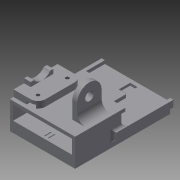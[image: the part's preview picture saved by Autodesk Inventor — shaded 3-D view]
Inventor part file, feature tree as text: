
AUTODESK INVENTOR PART (.ipt)
format: ipt  version: 2014 SP1 (Build 180222100, 222)  size: 471,040 bytes
history: native  units: mm
features: extrude x23, sketch x22, mirror x6, fillet x6, plane x2, hole x1, chamfer x1
ambient origin geometry x8: Origin, YZ Plane, XZ Plane, XY Plane, X Axis, Y Axis, Z Axis, Center Point
bodies: Solid1 (feature_tree)
feature tree (61):
  extrude  "Extrusion1"  Depth=40.0mm
  extrude  "Extrusion2"  Depth=10.0mm
  extrude  "Extrusion3"  Depth=8.5mm TaperAngle=0.0deg
  mirror  "Mirror1"
  extrude  "Extrusion4"  Depth=2.0mm TaperAngle=0.0deg
  mirror  "Mirror2"
  extrude  "Extrusion5"  Depth=2.0mm TaperAngle=0.0deg
  extrude  "Extrusion6"  Depth=12.5mm
  extrude  "Extrusion7"  Depth=12.5mm
  fillet  "Fillet1"  Radius=18.25mm
  extrude  "Extrusion8"  Depth=15.0mm
  plane  "Work Plane1"
  extrude  "Extrusion9"  Depth=5.0mm
  plane  "Work Plane2"
  mirror  "Mirror3"
  hole  "Hole1"  [1 undecoded]
  extrude  "Extrusion10"  Depth=7.5mm
  extrude  "Extrusion11"  Depth=7.5mm
  extrude  "Extrusion12"  Depth=5.0mm
  mirror  "Mirror4"
  fillet  "Fillet2"  Radius=4.0mm
  fillet  "Fillet3"  [1 undecoded]
  fillet  "Fillet4"  Radius=5.0mm
  extrude  "Extrusion13"  Depth=4.5mm
  sketch  "Sketch16"  dims[d45=4.5mm d46=9.0mm]
  extrude  "Extrusion14"  Depth=4.5mm
  extrude  "Extrusion15"  Depth=2.0mm
  extrude  "Extrusion17"  Depth=10.0mm TaperAngle=0.0deg
  extrude  "Extrusion16"  Depth=5.0mm TaperAngle=0.0deg
  chamfer  "Chamfer1"  Distance=2.0mm
  mirror  "Mirror5"
  extrude  "Extrusion18"  Depth=5.0mm
  extrude  "Extrusion19"  Depth=20.0mm TaperAngle=0.0deg
  fillet  "Fillet5"  Radius=37.0mm
  extrude  "Extrusion20"  Depth=40.0mm
  extrude  "Extrusion21"  Depth=1.5mm
  extrude  "Extrusion22"  Depth=4.5mm TaperAngle=0.0deg
  mirror  "Mirror6"
  fillet  "Fillet6"  Radius=4.5mm
  extrude  "Extrusion23"  Depth=15.0mm
  sketch  "Sketch1"  dims[d0=40.0mm d2=6.35mm]
  sketch  "Sketch2"  dims[d4=9.5mm d5=10.0mm]
  sketch  "Sketch4"  dims[d6=20.0mm d7=8.5mm d8=0.0mm]
  sketch  "Sketch5"  dims[d9=20.0mm d10=2.0mm d11=0.0mm]
  sketch  "Sketch6"  dims[d12=6.35mm d13=2.0mm d14=0.0mm]
  sketch  "Sketch7"  dims[d15=7.0mm d17=12.5mm]
  sketch  "Sketch9"  dims[d18=2.0mm d19=0.0mm d20=12.5mm d21=18.25mm d22=0.0mm]
  sketch  "Sketch10"  dims[d23=15.0mm d25=3.0mm]
  sketch  "Sketch11"  dims[d26=4.5mm d27=5.0mm]
  sketch  "Sketch12"  dims[d28=14.5mm d29=17.5mm d30=0.0mm]
  sketch  "Sketch13"  dims[d31=5.1mm d34=7.5mm]
  sketch  "Sketch14"  dims[d35=10.0mm d36=0.0mm d37=7.5mm]
  sketch  "Sketch15"  dims[d38=15.0mm d39=27.0mm d41=4.0mm d42=0.0mm d43=-2.0mm d44=5.0mm]
  sketch  "Sketch17"  dims[d47=2.0mm d48=0.0mm d49=4.5mm]
  sketch  "Sketch18"  dims[d50=18.0mm]
  sketch  "Sketch19"  dims[d51=2.013mm d52=6.0mm d53=4.0mm d54=2.0mm d55=90.0deg d56=4.0mm d57=20.594885mm d58=6.0mm]
  sketch  "Sketch20"  dims[d61=10.0mm d62=4.0mm d63=0.0mm]
  sketch  "Sketch21"  dims[d64=12.0mm d65=5.0mm d66=0.0mm d67=2.0mm d68=0.0mm]
  sketch  "Sketch23"  dims[d69=4.5mm d70=5.0mm]
  sketch  "Sketch24"  dims[d71=2.0mm d72=20.0mm d73=0.0mm d74=37.0mm]
  sketch  "Sketch25"  dims[d76=56.75mm d78=40.0mm d79=1.5mm d80=4.5mm d81=0.0mm d82=4.5mm d83=0.0mm d84=8.0mm d85=6.0mm d86=20.0mm d87=0.25mm d88=2.5mm d89=0.0mm d90=2.0mm d93=5.5mm d94=24.5mm d95=2.25mm d96=0.0mm d97=1.0mm d98=2.0mm d99=45.0deg d100=54.5mm d101=0.5mm d102=0.5mm d103=7.0mm d104=3.5mm d105=2.25mm d106=0.0mm d107=1.0mm d108=0.0mm d109=2.0mm d110=1.0mm d111=2.5mm d112=1.0mm d113=0.0mm d114=16.25mm d116=18.5mm d117=1.75mm d118=4.25mm d119=5.0mm d120=0.0mm d121=2.0mm d122=35.0mm d123=4.0mm d124=0.0mm d125=2.0mm d126=2.0mm d127=2.0mm d128=2.0mm d129=15.0mm d130=0.0mm]
note: 2 required parameter values undecoded (feature->parameter linkage not recoverable at this tier; creation-order binding heuristic only, values carry confidence <= 0.55)
